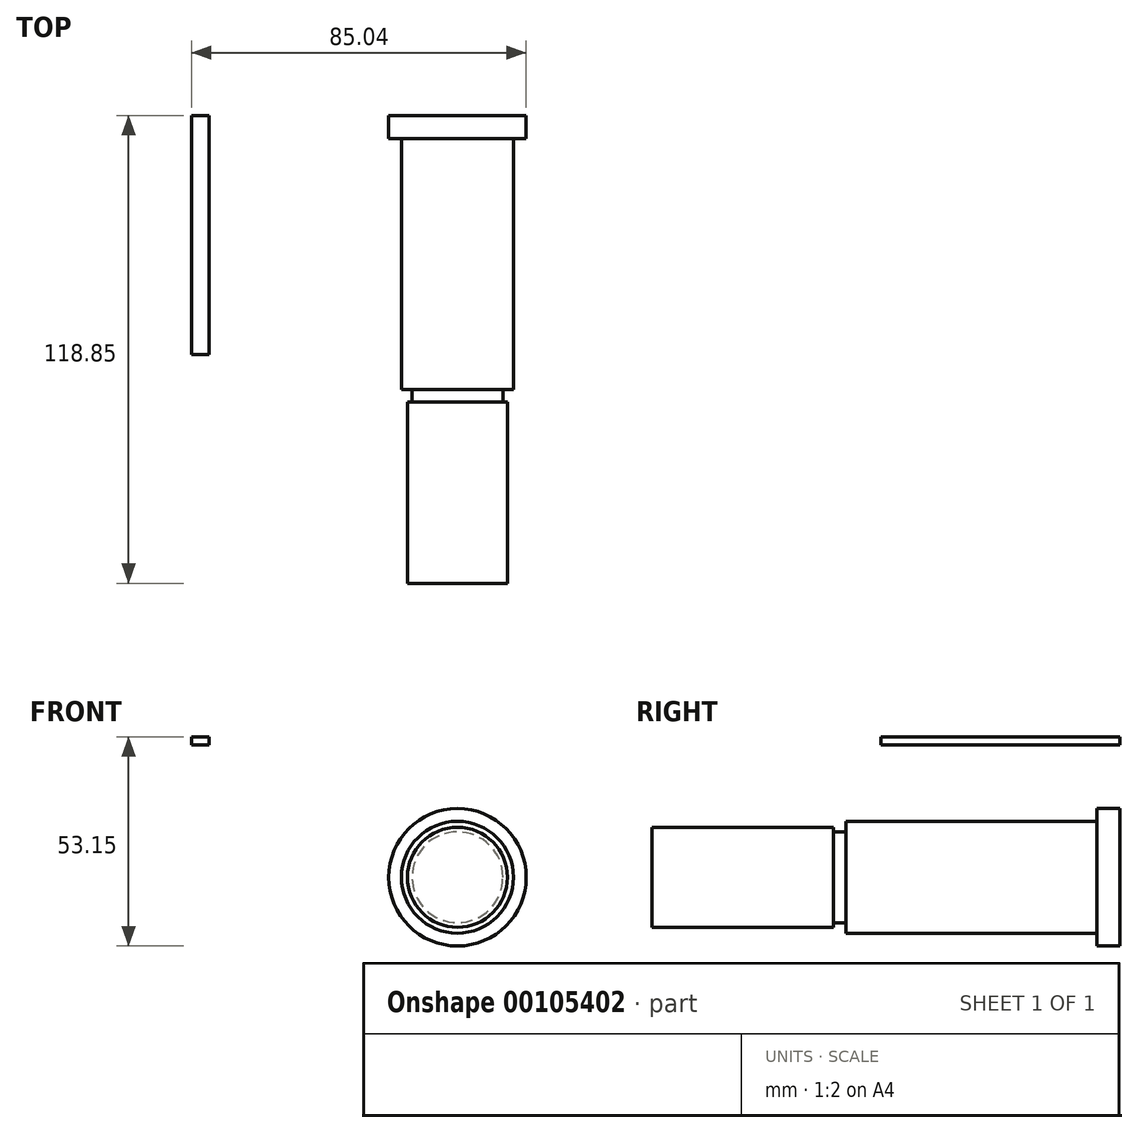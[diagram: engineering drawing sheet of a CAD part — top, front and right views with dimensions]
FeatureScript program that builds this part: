
annotation { "Feature Type Name" : "Feature", "Feature Type Description" : "" }
export const myFeature = defineFeature(function(context is Context, id is Id, definition is map)
    precondition{}
    {
        {
            var Q0;
            Q0=qCreatedBy(makeId("Front.planeOp"),FACE);
            var sketch = newSketch(context, id + "F0", { "sketchPlane" : qUnion([Q0])});
            skCircle(sketch, "E0", {"center": v(0, 0) * mm, "radius": 17.46 * mm});
            skSolve(sketch);
        }
        {
            var Q0;
            Q0=makeQuery(id+"F0.imprint","IMPRINT",FACE,{"disambiguationData":[TD([[makeQuery(id+"F0.imprint","IMPRINT",EDGE,{"derivedFrom":sQuery(id+"F0.wireOp",EDGE,"E0")}),1.0]])]});
            extrude(context, id + "F1", {"entities" : qUnion([Q0]), "depth" : 5.9 * mm});
        }
        {
            var Q0;
            Q0=makeQuery(id+"F1.opExtrude","CAP_FACE",FACE,{"disambiguationData":[OSD([sQuery(id+"F0.wireOp",EDGE,"E0")])],"isStart":false});
            var sketch = newSketch(context, id + "F2", { "sketchPlane" : qUnion([Q0])});
            skCircle(sketch, "E1", {"center": v(0, 0) * mm, "radius": 14.22 * mm});
            skSolve(sketch);
        }
        {
            var Q0;
            Q0=makeQuery(id+"F2.imprint","IMPRINT",FACE,{"disambiguationData":[TD([[makeQuery(id+"F2.imprint","IMPRINT",EDGE,{"derivedFrom":sQuery(id+"F2.wireOp",EDGE,"E1")}),1.0]])]});
            extrude(context, id + "F3", {"entities" : qUnion([Q0]), "operationType" : NewBodyOperationType.ADD, "depth" : 63.75 * mm});
        }
        {
            var Q0;
            Q0=makeQuery(id+"F3.opExtrude","CAP_FACE",FACE,{"disambiguationData":[OSD([sQuery(id+"F2.wireOp",EDGE,"E1")])],"isStart":false});
            var sketch = newSketch(context, id + "F4", { "sketchPlane" : qUnion([Q0])});
            skCircle(sketch, "E2", {"center": v(0, 0) * mm, "radius": 11.53 * mm});
            skSolve(sketch);
        }
        {
            var Q0;
            Q0=makeQuery(id+"F4.imprint","IMPRINT",FACE,{"disambiguationData":[TD([[makeQuery(id+"F4.imprint","IMPRINT",EDGE,{"derivedFrom":sQuery(id+"F4.wireOp",EDGE,"E2")}),1.0]])]});
            extrude(context, id + "F5", {"entities" : qUnion([Q0]), "operationType" : NewBodyOperationType.ADD, "depth" : 3.1 * mm});
        }
        {
            var Q0;
            Q0=makeQuery(id+"F5.opExtrude","CAP_FACE",FACE,{"disambiguationData":[OSD([sQuery(id+"F4.wireOp",EDGE,"E2")])],"isStart":false});
            var sketch = newSketch(context, id + "F6", { "sketchPlane" : qUnion([Q0])});
            skCircle(sketch, "E3", {"center": v(0, 0) * mm, "radius": 12.7 * mm});
            skSolve(sketch);
        }
        {
            var Q0;
            Q0 = qSketchRegion(id + "F6", true);
            extrude(context, id + "F7", {"entities" : qUnion([Q0]), "operationType" : NewBodyOperationType.ADD, "depth" : 46.1 * mm});
        }
        {
            var Q0;
            Q0=qCreatedBy(makeId("Front.planeOp"),FACE);
            var sketch = newSketch(context, id + "F8", { "sketchPlane" : qUnion([Q0])});
            skLineSegment(sketch, "E4.bottom", {"start": v(-63.14, 33.66) * mm, "end": v(-67.58, 33.66) * mm});
            skLineSegment(sketch, "E4.top", {"start": v(-63.14, 35.7) * mm, "end": v(-67.58, 35.7) * mm});
            skLineSegment(sketch, "E4.left", {"start": v(-63.14, 33.66) * mm, "end": v(-63.14, 35.7) * mm});
            skLineSegment(sketch, "E4.right", {"start": v(-67.58, 33.66) * mm, "end": v(-67.58, 35.7) * mm});
            skPoint(sketch, "E4.middle", {"position": v(-65.36, 34.68) * mm});
            skSolve(sketch);
        }
        {
            var Q0;
            Q0=makeQuery(id+"F8.imprint","IMPRINT",FACE,{"disambiguationData":[TD([[makeQuery(id+"F8.imprint","IMPRINT",EDGE,{"derivedFrom":sQuery(id+"F8.wireOp",EDGE,"E4.bottom")}),-1.0]])]});
            extrude(context, id + "F9", {"entities" : qUnion([Q0]), "depth" : 60.7 * mm});
        }
    });
